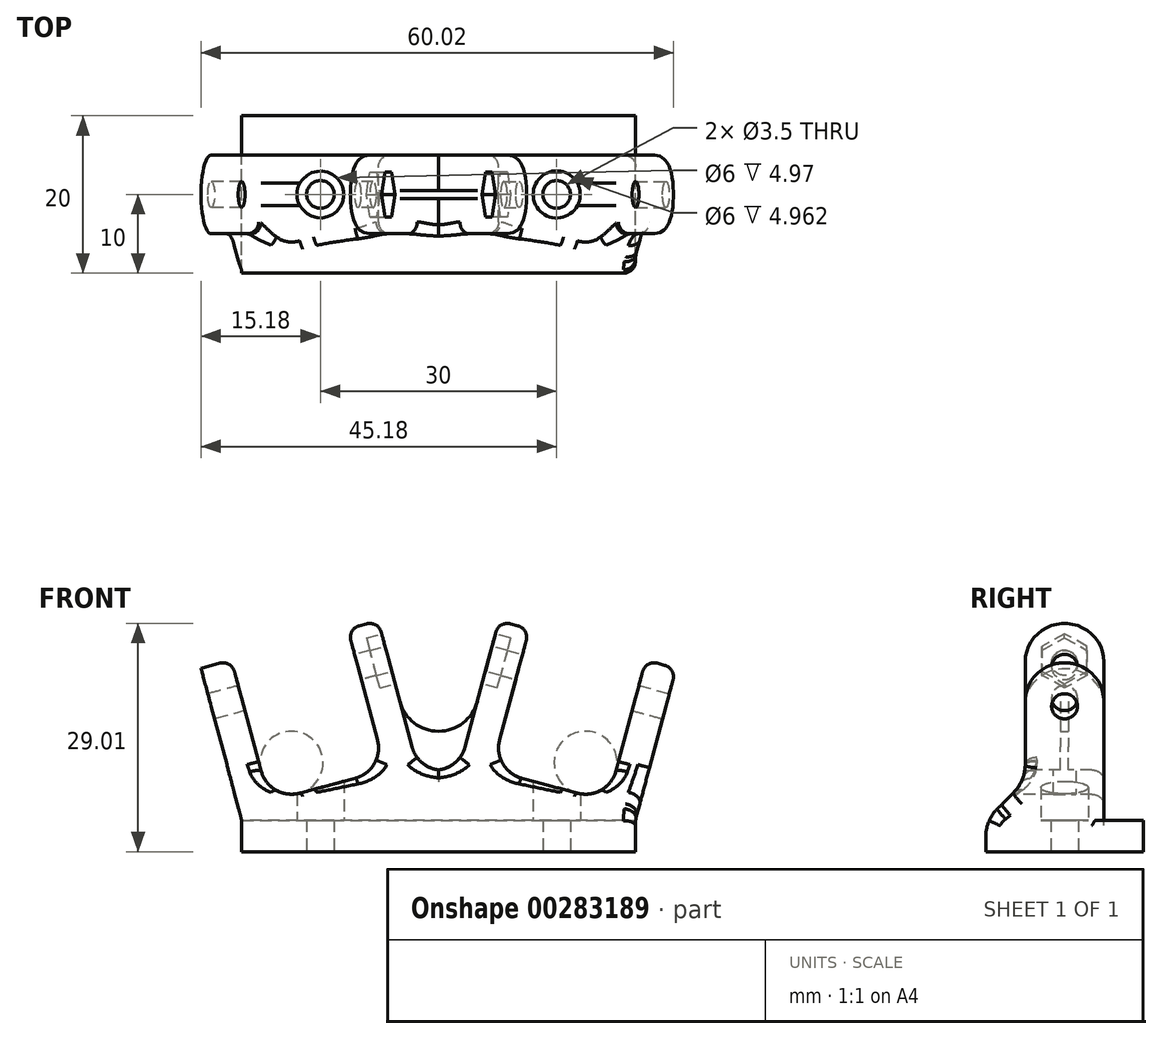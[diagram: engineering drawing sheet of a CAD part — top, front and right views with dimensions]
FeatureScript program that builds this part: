
annotation { "Feature Type Name" : "Feature", "Feature Type Description" : "" }
export const myFeature = defineFeature(function(context is Context, id is Id, definition is map)
    precondition{}
    {
        {
            var Q0;
            Q0=qCreatedBy(makeId("Top.planeOp"),FACE);
            var sketch = newSketch(context, id + "F0", { "sketchPlane" : qUnion([Q0])});
            skLineSegment(sketch, "E0.bottom", {"start": v(0, 0) * mm, "end": v(50, 0) * mm});
            skLineSegment(sketch, "E0.top", {"start": v(0, 20) * mm, "end": v(50, 20) * mm});
            skLineSegment(sketch, "E0.left", {"start": v(0, 0) * mm, "end": v(0, 20) * mm});
            skLineSegment(sketch, "E0.right", {"start": v(50, 0) * mm, "end": v(50, 20) * mm});
            skSolve(sketch);
        }
        {
            var Q0;
            Q0 = qSketchRegion(id + "F0", true);
            extrude(context, id + "F1", {"entities" : qUnion([Q0]), "depth" : 4 * mm});
        }
        {
            var Q0;
            Q0=makeQuery(id+"F1.opExtrude","SWEPT_FACE",FACE,{"disambiguationData":[OSD([sQuery(id+"F0.wireOp",EDGE,"E0.bottom")])]});
            cPlane(context, id + "F2", {"entities" : qUnion([Q0]), "cplaneType" : CPlaneType.OFFSET, "offset" : 10 * mm, "oppositeDirection" : true, "width" : 150 * mm, "height" : 150 * mm});
        }
        {
            var Q0;
            Q0=qCreatedBy(id+"F2.planeOp",FACE);
            var sketch = newSketch(context, id + "F3", { "sketchPlane" : qUnion([Q0])});
            skLineSegment(sketch, "E1.0.0", {"start": v(0, 0) * mm, "end": v(50, 0) * mm, "construction": true});
            skLineSegment(sketch, "E1.0.1", {"start": v(50, 0) * mm, "end": v(50, 4) * mm, "construction": true});
            skLineSegment(sketch, "E1.0.2", {"start": v(50, 4) * mm, "end": v(0, 4) * mm, "construction": true});
            skLineSegment(sketch, "E1.0.3", {"start": v(0, 4) * mm, "end": v(0, 0) * mm, "construction": true});
            skLineSegment(sketch, "E2", {"start": v(0, 4) * mm, "end": v(-5.18, 23.32) * mm});
            skLineSegment(sketch, "E3", {"start": v(-5.18, 23.32) * mm, "end": v(-1.31, 24.35) * mm});
            skLineSegment(sketch, "E4", {"start": v(-1.31, 24.35) * mm, "end": v(3.5, 6.41) * mm});
            skLineSegment(sketch, "E5", {"start": v(4.14, 4) * mm, "end": v(0, 4) * mm});
            skLineSegment(sketch, "E6", {"start": v(25, 4) * mm, "end": v(25, 45.14) * mm, "construction": true});
            skLineSegment(sketch, "E7", {"start": v(-5.18, 23.32) * mm, "end": v(32.1, 33.3) * mm, "construction": true});
            skLineSegment(sketch, "E8", {"start": v(22.41, 10.37) * mm, "end": v(17.33, 29.35) * mm});
            skLineSegment(sketch, "E9", {"start": v(17.33, 29.35) * mm, "end": v(13.47, 28.31) * mm});
            skLineSegment(sketch, "E10", {"start": v(13.47, 28.31) * mm, "end": v(18.27, 10.37) * mm});
            skLineSegment(sketch, "E11", {"start": v(19.98, 4) * mm, "end": v(24.12, 4) * mm});
            skLineSegment(sketch, "E12", {"start": v(3.5, 6.41) * mm, "end": v(18.27, 10.37) * mm});
            skLineSegment(sketch, "E13", {"start": v(4.14, 4) * mm, "end": v(19.98, 4) * mm});
            skLineSegment(sketch, "E14.MirrorCS", {"start": v(45.86, 4) * mm, "end": v(30.02, 4) * mm});
            skLineSegment(sketch, "E15.MirrorCS", {"start": v(36.53, 28.31) * mm, "end": v(31.73, 10.37) * mm});
            skLineSegment(sketch, "E16.MirrorCS", {"start": v(32.67, 29.35) * mm, "end": v(36.53, 28.31) * mm});
            skLineSegment(sketch, "E17.MirrorCS", {"start": v(46.5, 6.41) * mm, "end": v(31.73, 10.37) * mm});
            skLineSegment(sketch, "E18.MirrorCS", {"start": v(55.18, 23.32) * mm, "end": v(51.31, 24.35) * mm});
            skLineSegment(sketch, "E19.MirrorCS", {"start": v(45.86, 4) * mm, "end": v(50, 4) * mm});
            skLineSegment(sketch, "E20.MirrorCS", {"start": v(30.02, 4) * mm, "end": v(25.88, 4) * mm});
            skLineSegment(sketch, "E21.MirrorCS", {"start": v(51.31, 24.35) * mm, "end": v(46.5, 6.41) * mm});
            skLineSegment(sketch, "E22.MirrorCS", {"start": v(50, 4) * mm, "end": v(55.18, 23.32) * mm});
            skLineSegment(sketch, "E23.MirrorCS", {"start": v(27.59, 10.37) * mm, "end": v(32.67, 29.35) * mm});
            skLineSegment(sketch, "E24", {"start": v(22.41, 10.37) * mm, "end": v(27.59, 10.37) * mm});
            skLineSegment(sketch, "E25", {"start": v(24.12, 4) * mm, "end": v(25.88, 4) * mm});
            skSolve(sketch);
        }
        {
            var Q0;
            Q0 = qSketchRegion(id + "F3", true);
            extrude(context, id + "F4", {"entities" : qUnion([Q0]), "operationType" : NewBodyOperationType.ADD, "endBound" : BoundingType.SYMMETRIC, "depth" : 10 * mm});
        }
        {
            var Q0;
            Q0=makeQuery(id+"F4.opExtrude","SWEPT_FACE",FACE,{"disambiguationData":[OSD([sQuery(id+"F3.wireOp",EDGE,"E2")])]});
            var sketch = newSketch(context, id + "F5", { "sketchPlane" : qUnion([Q0])});
            skCircle(sketch, "E26", {"center": v(-10, 18.86) * mm, "radius": 1.65 * mm});
            skPoint(sketch, "E26.centerSnap0", {"position": v(-10, 23.86) * mm});
            skSolve(sketch);
        }
        {
            var Q0;
            Q0 = qSketchRegion(id + "F5", true);
            var Q1;
            Q1=makeQuery(id+"F4.opExtrude","SWEPT_FACE",FACE,{"disambiguationData":[OSD([sQuery(id+"F3.wireOp",EDGE,"E8")])]});
            extrude(context, id + "F6", {"entities" : qUnion([Q0]), "operationType" : NewBodyOperationType.REMOVE, "endBound" : BoundingType.UP_TO_SURFACE, "oppositeDirection" : true, "endBoundEntityFace" : qUnion([Q1]), "depth" : 25 * mm});
        }
        {
            var Q0;
            Q0=makeQuery(id+"F4.opExtrude","SWEPT_FACE",FACE,{"disambiguationData":[OSD([sQuery(id+"F3.wireOp",EDGE,"E22.MirrorCS")])]});
            var sketch = newSketch(context, id + "F7", { "sketchPlane" : qUnion([Q0])});
            skCircle(sketch, "E27", {"center": v(10, 31.8) * mm, "radius": 1.65 * mm});
            skPoint(sketch, "E27.centerSnap0", {"position": v(10, 36.8) * mm});
            skSolve(sketch);
        }
        {
            var Q0;
            Q0 = qSketchRegion(id + "F7", true);
            var Q1;
            Q1=makeQuery(id+"F4.opExtrude","SWEPT_FACE",FACE,{"disambiguationData":[OSD([sQuery(id+"F3.wireOp",EDGE,"E23.MirrorCS")])]});
            extrude(context, id + "F8", {"entities" : qUnion([Q0]), "operationType" : NewBodyOperationType.REMOVE, "endBound" : BoundingType.UP_TO_SURFACE, "oppositeDirection" : true, "endBoundEntityFace" : qUnion([Q1]), "depth" : 25 * mm});
        }
        {
            var Q0;
            Q0=makeQuery(id+"F4.opExtrude","CAP_EDGE",EDGE,{"disambiguationData":[OSD([sQuery(id+"F3.wireOp",EDGE,"E5"),sQuery(id+"F3.wireOp",EDGE,"E11"),sQuery(id+"F3.wireOp",EDGE,"E13"),sQuery(id+"F3.wireOp",EDGE,"E14.MirrorCS"),sQuery(id+"F3.wireOp",EDGE,"E19.MirrorCS"),sQuery(id+"F3.wireOp",EDGE,"E20.MirrorCS"),sQuery(id+"F3.wireOp",EDGE,"E25")])],"isStart":false});
            var Q1;
            Q1=makeQuery(id+"F4.opExtrude","CAP_EDGE",EDGE,{"disambiguationData":[OSD([sQuery(id+"F3.wireOp",EDGE,"E5"),sQuery(id+"F3.wireOp",EDGE,"E11"),sQuery(id+"F3.wireOp",EDGE,"E13"),sQuery(id+"F3.wireOp",EDGE,"E14.MirrorCS"),sQuery(id+"F3.wireOp",EDGE,"E19.MirrorCS"),sQuery(id+"F3.wireOp",EDGE,"E20.MirrorCS"),sQuery(id+"F3.wireOp",EDGE,"E25")])],"isStart":true});
            chamfer(context, id + "F9", {"entities" : qUnion([Q0, Q1]), "width" : 5 * mm, "tangentPropagation" : true});
        }
        {
            var Q0;
            Q0=makeQuery(id+"F4.boolean.opBoolean","MERGE",EDGE,{"derivedFrom":[makeQuery(id+"F1.opExtrude","CAP_EDGE",EDGE,{"disambiguationData":[OSD([sQuery(id+"F0.wireOp",EDGE,"E0.right")])],"isStart":false}),makeQuery(id+"F4.opExtrude","SWEPT_EDGE",EDGE,{"disambiguationData":[OSD([sQuery(id+"F3.wireOp",EDGE,"E19.MirrorCS"),sQuery(id+"F3.wireOp",EDGE,"E22.MirrorCS")])]})]});
            var Q1;
            Q1=makeQuery(id+"F4.boolean.opBoolean","MERGE",EDGE,{"derivedFrom":[makeQuery(id+"F1.opExtrude","CAP_EDGE",EDGE,{"disambiguationData":[OSD([sQuery(id+"F0.wireOp",EDGE,"E0.left")])],"isStart":false}),makeQuery(id+"F4.opExtrude","SWEPT_EDGE",EDGE,{"disambiguationData":[OSD([sQuery(id+"F3.wireOp",EDGE,"E2"),sQuery(id+"F3.wireOp",EDGE,"E5")])]})]});
            fillet(context, id + "F10", {"entities" : qUnion([Q0, Q1]), "radius" : 5 * mm, "tangentPropagation" : true, "allowEdgeOverflow" : false});
        }
        {
            var Q0;
            Q0=makeQuery(id+"F1.opExtrude","CAP_FACE",FACE,{"disambiguationData":[OSD([sQuery(id+"F0.wireOp",EDGE,"E0.bottom"),sQuery(id+"F0.wireOp",EDGE,"E0.top"),sQuery(id+"F0.wireOp",EDGE,"E0.left"),sQuery(id+"F0.wireOp",EDGE,"E0.right")])],"isStart":true});
            var sketch = newSketch(context, id + "F11", { "sketchPlane" : qUnion([Q0])});
            skCircle(sketch, "E28", {"center": v(10, -10) * mm, "radius": 1.75 * mm});
            skPoint(sketch, "E28.centerSnap0", {"position": v(0, -10) * mm});
            skCircle(sketch, "E29", {"center": v(40, -10) * mm, "radius": 1.75 * mm});
            skSolve(sketch);
        }
        {
            var Q0;
            Q0 = qSketchRegion(id + "F11", true);
            extrude(context, id + "F12", {"entities" : qUnion([Q0]), "operationType" : NewBodyOperationType.REMOVE, "endBound" : BoundingType.UP_TO_NEXT, "oppositeDirection" : true, "depth" : 25 * mm});
        }
        {
            var Q0;
            Q0=makeQuery(id+"F1.opExtrude","CAP_FACE",FACE,{"disambiguationData":[OSD([sQuery(id+"F0.wireOp",EDGE,"E0.bottom"),sQuery(id+"F0.wireOp",EDGE,"E0.top"),sQuery(id+"F0.wireOp",EDGE,"E0.left"),sQuery(id+"F0.wireOp",EDGE,"E0.right")])],"isStart":true});
            cPlane(context, id + "F13", {"entities" : qUnion([Q0]), "cplaneType" : CPlaneType.OFFSET, "offset" : 4 * mm, "oppositeDirection" : true, "width" : 150 * mm, "height" : 150 * mm});
        }
        {
            var Q0;
            Q0=qCreatedBy(id+"F13.planeOp",FACE);
            var sketch = newSketch(context, id + "F14", { "sketchPlane" : qUnion([Q0])});
            skCircle(sketch, "E30.0", {"center": v(10, -10) * mm, "radius": 1.75 * mm, "construction": true});
            skCircle(sketch, "E31.0", {"center": v(40, -10) * mm, "radius": 1.75 * mm, "construction": true});
            skCircle(sketch, "E32", {"center": v(10, -10) * mm, "radius": 3 * mm});
            skCircle(sketch, "E33", {"center": v(40, -10) * mm, "radius": 3 * mm});
            skSolve(sketch);
        }
        {
            var Q0;
            Q0 = qSketchRegion(id + "F14", true);
            extrude(context, id + "F15", {"entities" : qUnion([Q0]), "operationType" : NewBodyOperationType.REMOVE, "oppositeDirection" : true, "depth" : 20 * mm});
        }
        {
            var Q0;
            Q0=makeQuery(id+"F4.opExtrude","CAP_EDGE",EDGE,{"disambiguationData":[OSD([sQuery(id+"F3.wireOp",EDGE,"E3")])],"isStart":true});
            var Q1;
            Q1=makeQuery(id+"F4.opExtrude","CAP_EDGE",EDGE,{"disambiguationData":[OSD([sQuery(id+"F3.wireOp",EDGE,"E3")])],"isStart":false});
            var Q2;
            Q2=makeQuery(id+"F4.opExtrude","CAP_EDGE",EDGE,{"disambiguationData":[OSD([sQuery(id+"F3.wireOp",EDGE,"E9")])],"isStart":true});
            var Q3;
            Q3=makeQuery(id+"F4.opExtrude","CAP_EDGE",EDGE,{"disambiguationData":[OSD([sQuery(id+"F3.wireOp",EDGE,"E9")])],"isStart":false});
            var Q4;
            Q4=makeQuery(id+"F4.opExtrude","CAP_EDGE",EDGE,{"disambiguationData":[OSD([sQuery(id+"F3.wireOp",EDGE,"E16.MirrorCS")])],"isStart":true});
            var Q5;
            Q5=makeQuery(id+"F4.opExtrude","CAP_EDGE",EDGE,{"disambiguationData":[OSD([sQuery(id+"F3.wireOp",EDGE,"E16.MirrorCS")])],"isStart":false});
            var Q6;
            Q6=makeQuery(id+"F4.opExtrude","CAP_EDGE",EDGE,{"disambiguationData":[OSD([sQuery(id+"F3.wireOp",EDGE,"E18.MirrorCS")])],"isStart":false});
            var Q7;
            Q7=makeQuery(id+"F4.opExtrude","CAP_EDGE",EDGE,{"disambiguationData":[OSD([sQuery(id+"F3.wireOp",EDGE,"E18.MirrorCS")])],"isStart":true});
            fillet(context, id + "F16", {"entities" : qUnion([Q0, Q1, Q2, Q3, Q4, Q5, Q6, Q7]), "radius" : 5 * mm, "tangentPropagation" : true, "allowEdgeOverflow" : false});
        }
        {
            var Q0;
            Q0=makeQuery(id+"F4.opExtrude","SWEPT_FACE",FACE,{"disambiguationData":[OSD([sQuery(id+"F3.wireOp",EDGE,"E8")])]});
            var sketch = newSketch(context, id + "F17", { "sketchPlane" : qUnion([Q0])});
            skCircle(sketch, "E34.cCircle", {"center": v(10, 18.86) * mm, "radius": 2.85 * mm, "construction": true});
            skLineSegment(sketch, "E34.0", {"start": v(10, 22.15) * mm, "end": v(12.85, 20.5) * mm});
            skLineSegment(sketch, "E34.1", {"start": v(12.85, 20.5) * mm, "end": v(12.85, 17.22) * mm});
            skLineSegment(sketch, "E34.2", {"start": v(12.85, 17.22) * mm, "end": v(10, 15.57) * mm});
            skLineSegment(sketch, "E34.3", {"start": v(10, 15.57) * mm, "end": v(7.15, 17.22) * mm});
            skLineSegment(sketch, "E34.4", {"start": v(7.15, 17.22) * mm, "end": v(7.15, 20.5) * mm});
            skLineSegment(sketch, "E34.5", {"start": v(7.15, 20.5) * mm, "end": v(10, 22.15) * mm});
            skPoint(sketch, "E34.0.midPoint", {"position": v(11.42, 21.33) * mm});
            skSolve(sketch);
        }
        {
            var Q0;
            Q0 = qSketchRegion(id + "F17", true);
            extrude(context, id + "F18", {"entities" : qUnion([Q0]), "operationType" : NewBodyOperationType.REMOVE, "oppositeDirection" : true, "depth" : 2 * mm});
        }
        {
            var Q0;
            Q0=makeQuery(id+"F4.opExtrude","SWEPT_FACE",FACE,{"disambiguationData":[OSD([sQuery(id+"F3.wireOp",EDGE,"E23.MirrorCS")])]});
            var sketch = newSketch(context, id + "F19", { "sketchPlane" : qUnion([Q0])});
            skCircle(sketch, "E35.cCircle", {"center": v(-10, 31.8) * mm, "radius": 2.85 * mm, "construction": true});
            skLineSegment(sketch, "E35.0", {"start": v(-7.15, 33.45) * mm, "end": v(-7.15, 30.16) * mm});
            skLineSegment(sketch, "E35.1", {"start": v(-7.15, 30.16) * mm, "end": v(-10, 28.51) * mm});
            skLineSegment(sketch, "E35.2", {"start": v(-10, 28.51) * mm, "end": v(-12.85, 30.16) * mm});
            skLineSegment(sketch, "E35.3", {"start": v(-12.85, 30.16) * mm, "end": v(-12.85, 33.45) * mm});
            skLineSegment(sketch, "E35.4", {"start": v(-12.85, 33.45) * mm, "end": v(-10, 35.1) * mm});
            skLineSegment(sketch, "E35.5", {"start": v(-10, 35.1) * mm, "end": v(-7.15, 33.45) * mm});
            skPoint(sketch, "E35.0.midPoint", {"position": v(-7.15, 31.8) * mm});
            skSolve(sketch);
        }
        {
            var Q0;
            Q0 = qSketchRegion(id + "F19", true);
            extrude(context, id + "F20", {"entities" : qUnion([Q0]), "operationType" : NewBodyOperationType.REMOVE, "oppositeDirection" : true, "depth" : 2 * mm});
        }
        {
            var Q0;
            Q0=makeQuery(id+"F9.opChamfer","BLEND_EDGE",EDGE,{"blendedFrom":[makeQuery(id+"F4.opExtrude","CAP_EDGE",EDGE,{"disambiguationData":[OSD([sQuery(id+"F3.wireOp",EDGE,"E5"),sQuery(id+"F3.wireOp",EDGE,"E11"),sQuery(id+"F3.wireOp",EDGE,"E13"),sQuery(id+"F3.wireOp",EDGE,"E14.MirrorCS"),sQuery(id+"F3.wireOp",EDGE,"E19.MirrorCS"),sQuery(id+"F3.wireOp",EDGE,"E20.MirrorCS"),sQuery(id+"F3.wireOp",EDGE,"E25")])],"isStart":false}),makeQuery(id+"F1.opExtrude","SWEPT_FACE",FACE,{"disambiguationData":[OSD([sQuery(id+"F0.wireOp",EDGE,"E0.bottom")])]})],"blendedInto":[makeQuery(id+"F1.opExtrude","SWEPT_FACE",FACE,{"disambiguationData":[OSD([sQuery(id+"F0.wireOp",EDGE,"E0.bottom")])]})]});
            var Q1;
            Q1=makeQuery(id+"F9.opChamfer","BLEND_EDGE",EDGE,{"blendedFrom":[makeQuery(id+"F4.opExtrude","CAP_EDGE",EDGE,{"disambiguationData":[OSD([sQuery(id+"F3.wireOp",EDGE,"E5"),sQuery(id+"F3.wireOp",EDGE,"E11"),sQuery(id+"F3.wireOp",EDGE,"E13"),sQuery(id+"F3.wireOp",EDGE,"E14.MirrorCS"),sQuery(id+"F3.wireOp",EDGE,"E19.MirrorCS"),sQuery(id+"F3.wireOp",EDGE,"E20.MirrorCS"),sQuery(id+"F3.wireOp",EDGE,"E25")])],"isStart":true}),makeQuery(id+"F1.opExtrude","SWEPT_FACE",FACE,{"disambiguationData":[OSD([sQuery(id+"F0.wireOp",EDGE,"E0.top")])]})],"blendedInto":[makeQuery(id+"F1.opExtrude","SWEPT_FACE",FACE,{"disambiguationData":[OSD([sQuery(id+"F0.wireOp",EDGE,"E0.top")])]})]});
            var Q2;
            {var subQ0=sQuery(id+"F3.wireOp",EDGE,"E25");var subQ1=sQuery(id+"F3.wireOp",EDGE,"E20.MirrorCS");var subQ2=sQuery(id+"F3.wireOp",EDGE,"E19.MirrorCS");var subQ3=sQuery(id+"F3.wireOp",EDGE,"E14.MirrorCS");var subQ4=sQuery(id+"F3.wireOp",EDGE,"E13");var subQ5=sQuery(id+"F3.wireOp",EDGE,"E11");var subQ6=sQuery(id+"F3.wireOp",EDGE,"E5");Q2=makeQuery(id+"F9.opChamfer","BLEND_EDGE",EDGE,{"disambiguationData":[OD(0.0)],"blendedFrom":[makeQuery(id+"F4.opExtrude","CAP_EDGE",EDGE,{"disambiguationData":[OSD([subQ6,subQ5,subQ4,subQ3,subQ2,subQ1,subQ0])],"isStart":false}),makeQuery(id+"F4.opExtrude","CAP_FACE",FACE,{"disambiguationData":[OSD([sQuery(id+"F3.wireOp",EDGE,"E2"),sQuery(id+"F3.wireOp",EDGE,"E3"),sQuery(id+"F3.wireOp",EDGE,"E4"),subQ6,sQuery(id+"F3.wireOp",EDGE,"E8"),sQuery(id+"F3.wireOp",EDGE,"E9"),sQuery(id+"F3.wireOp",EDGE,"E10"),subQ5,sQuery(id+"F3.wireOp",EDGE,"E12"),subQ4,subQ3,sQuery(id+"F3.wireOp",EDGE,"E15.MirrorCS"),sQuery(id+"F3.wireOp",EDGE,"E16.MirrorCS"),sQuery(id+"F3.wireOp",EDGE,"E17.MirrorCS"),sQuery(id+"F3.wireOp",EDGE,"E18.MirrorCS"),subQ2,subQ1,sQuery(id+"F3.wireOp",EDGE,"E21.MirrorCS"),sQuery(id+"F3.wireOp",EDGE,"E22.MirrorCS"),sQuery(id+"F3.wireOp",EDGE,"E23.MirrorCS"),sQuery(id+"F3.wireOp",EDGE,"E24"),subQ0])],"isStart":false})],"blendedInto":[makeQuery(id+"F4.opExtrude","CAP_FACE",FACE,{"disambiguationData":[OSD([sQuery(id+"F3.wireOp",EDGE,"E2"),sQuery(id+"F3.wireOp",EDGE,"E3"),sQuery(id+"F3.wireOp",EDGE,"E4"),subQ6,sQuery(id+"F3.wireOp",EDGE,"E8"),sQuery(id+"F3.wireOp",EDGE,"E9"),sQuery(id+"F3.wireOp",EDGE,"E10"),subQ5,sQuery(id+"F3.wireOp",EDGE,"E12"),subQ4,subQ3,sQuery(id+"F3.wireOp",EDGE,"E15.MirrorCS"),sQuery(id+"F3.wireOp",EDGE,"E16.MirrorCS"),sQuery(id+"F3.wireOp",EDGE,"E17.MirrorCS"),sQuery(id+"F3.wireOp",EDGE,"E18.MirrorCS"),subQ2,subQ1,sQuery(id+"F3.wireOp",EDGE,"E21.MirrorCS"),sQuery(id+"F3.wireOp",EDGE,"E22.MirrorCS"),sQuery(id+"F3.wireOp",EDGE,"E23.MirrorCS"),sQuery(id+"F3.wireOp",EDGE,"E24"),subQ0])],"isStart":false})]});}
            var Q3;
            {var subQ0=sQuery(id+"F3.wireOp",EDGE,"E25");var subQ1=sQuery(id+"F3.wireOp",EDGE,"E20.MirrorCS");var subQ2=sQuery(id+"F3.wireOp",EDGE,"E19.MirrorCS");var subQ3=sQuery(id+"F3.wireOp",EDGE,"E14.MirrorCS");var subQ4=sQuery(id+"F3.wireOp",EDGE,"E13");var subQ5=sQuery(id+"F3.wireOp",EDGE,"E11");var subQ6=sQuery(id+"F3.wireOp",EDGE,"E5");Q3=makeQuery(id+"F9.opChamfer","BLEND_EDGE",EDGE,{"disambiguationData":[OD(0.0)],"blendedFrom":[makeQuery(id+"F4.opExtrude","CAP_EDGE",EDGE,{"disambiguationData":[OSD([subQ6,subQ5,subQ4,subQ3,subQ2,subQ1,subQ0])],"isStart":true}),makeQuery(id+"F4.opExtrude","CAP_FACE",FACE,{"disambiguationData":[OSD([sQuery(id+"F3.wireOp",EDGE,"E2"),sQuery(id+"F3.wireOp",EDGE,"E3"),sQuery(id+"F3.wireOp",EDGE,"E4"),subQ6,sQuery(id+"F3.wireOp",EDGE,"E8"),sQuery(id+"F3.wireOp",EDGE,"E9"),sQuery(id+"F3.wireOp",EDGE,"E10"),subQ5,sQuery(id+"F3.wireOp",EDGE,"E12"),subQ4,subQ3,sQuery(id+"F3.wireOp",EDGE,"E15.MirrorCS"),sQuery(id+"F3.wireOp",EDGE,"E16.MirrorCS"),sQuery(id+"F3.wireOp",EDGE,"E17.MirrorCS"),sQuery(id+"F3.wireOp",EDGE,"E18.MirrorCS"),subQ2,subQ1,sQuery(id+"F3.wireOp",EDGE,"E21.MirrorCS"),sQuery(id+"F3.wireOp",EDGE,"E22.MirrorCS"),sQuery(id+"F3.wireOp",EDGE,"E23.MirrorCS"),sQuery(id+"F3.wireOp",EDGE,"E24"),subQ0])],"isStart":true})],"blendedInto":[makeQuery(id+"F4.opExtrude","CAP_FACE",FACE,{"disambiguationData":[OSD([sQuery(id+"F3.wireOp",EDGE,"E2"),sQuery(id+"F3.wireOp",EDGE,"E3"),sQuery(id+"F3.wireOp",EDGE,"E4"),subQ6,sQuery(id+"F3.wireOp",EDGE,"E8"),sQuery(id+"F3.wireOp",EDGE,"E9"),sQuery(id+"F3.wireOp",EDGE,"E10"),subQ5,sQuery(id+"F3.wireOp",EDGE,"E12"),subQ4,subQ3,sQuery(id+"F3.wireOp",EDGE,"E15.MirrorCS"),sQuery(id+"F3.wireOp",EDGE,"E16.MirrorCS"),sQuery(id+"F3.wireOp",EDGE,"E17.MirrorCS"),sQuery(id+"F3.wireOp",EDGE,"E18.MirrorCS"),subQ2,subQ1,sQuery(id+"F3.wireOp",EDGE,"E21.MirrorCS"),sQuery(id+"F3.wireOp",EDGE,"E22.MirrorCS"),sQuery(id+"F3.wireOp",EDGE,"E23.MirrorCS"),sQuery(id+"F3.wireOp",EDGE,"E24"),subQ0])],"isStart":true})]});}
            fillet(context, id + "F21", {"entities" : qUnion([Q0, Q1, Q2, Q3]), "radius" : 5 * mm, "tangentPropagation" : true, "allowEdgeOverflow" : false});
        }
        {
            var Q0;
            Q0=makeQuery(id+"F4.opExtrude","SWEPT_EDGE",EDGE,{"disambiguationData":[OSD([sQuery(id+"F3.wireOp",EDGE,"E4"),sQuery(id+"F3.wireOp",EDGE,"E12")])]});
            var Q1;
            Q1=makeQuery(id+"F4.opExtrude","SWEPT_EDGE",EDGE,{"disambiguationData":[OSD([sQuery(id+"F3.wireOp",EDGE,"E10"),sQuery(id+"F3.wireOp",EDGE,"E12")])]});
            var Q2;
            Q2=makeQuery(id+"F4.opExtrude","SWEPT_EDGE",EDGE,{"disambiguationData":[OSD([sQuery(id+"F3.wireOp",EDGE,"E23.MirrorCS"),sQuery(id+"F3.wireOp",EDGE,"E24")])]});
            var Q3;
            Q3=makeQuery(id+"F4.opExtrude","SWEPT_EDGE",EDGE,{"disambiguationData":[OSD([sQuery(id+"F3.wireOp",EDGE,"E17.MirrorCS"),sQuery(id+"F3.wireOp",EDGE,"E21.MirrorCS")])]});
            var Q4;
            Q4=makeQuery(id+"F4.opExtrude","SWEPT_EDGE",EDGE,{"disambiguationData":[OSD([sQuery(id+"F3.wireOp",EDGE,"E8"),sQuery(id+"F3.wireOp",EDGE,"E24")])]});
            var Q5;
            Q5=makeQuery(id+"F4.opExtrude","SWEPT_EDGE",EDGE,{"disambiguationData":[OSD([sQuery(id+"F3.wireOp",EDGE,"E15.MirrorCS"),sQuery(id+"F3.wireOp",EDGE,"E17.MirrorCS")])]});
            fillet(context, id + "F22", {"entities" : qUnion([Q0, Q1, Q2, Q3, Q4, Q5]), "radius" : 4 * mm, "tangentPropagation" : true, "allowEdgeOverflow" : false});
        }
        {
            var Q0;
            {var subQ0=sQuery(id+"F3.wireOp",EDGE,"E25");var subQ1=sQuery(id+"F3.wireOp",EDGE,"E20.MirrorCS");var subQ2=sQuery(id+"F3.wireOp",EDGE,"E19.MirrorCS");var subQ3=sQuery(id+"F3.wireOp",EDGE,"E14.MirrorCS");var subQ4=sQuery(id+"F3.wireOp",EDGE,"E13");var subQ5=sQuery(id+"F3.wireOp",EDGE,"E11");var subQ6=sQuery(id+"F3.wireOp",EDGE,"E5");Q0=makeQuery(id+"F9.opChamfer","BLEND_EDGE",EDGE,{"disambiguationData":[OD(2.0)],"blendedFrom":[makeQuery(id+"F4.opExtrude","CAP_EDGE",EDGE,{"disambiguationData":[OSD([subQ6,subQ5,subQ4,subQ3,subQ2,subQ1,subQ0])],"isStart":false}),makeQuery(id+"F4.opExtrude","CAP_FACE",FACE,{"disambiguationData":[OSD([sQuery(id+"F3.wireOp",EDGE,"E2"),sQuery(id+"F3.wireOp",EDGE,"E3"),sQuery(id+"F3.wireOp",EDGE,"E4"),subQ6,sQuery(id+"F3.wireOp",EDGE,"E8"),sQuery(id+"F3.wireOp",EDGE,"E9"),sQuery(id+"F3.wireOp",EDGE,"E10"),subQ5,sQuery(id+"F3.wireOp",EDGE,"E12"),subQ4,subQ3,sQuery(id+"F3.wireOp",EDGE,"E15.MirrorCS"),sQuery(id+"F3.wireOp",EDGE,"E16.MirrorCS"),sQuery(id+"F3.wireOp",EDGE,"E17.MirrorCS"),sQuery(id+"F3.wireOp",EDGE,"E18.MirrorCS"),subQ2,subQ1,sQuery(id+"F3.wireOp",EDGE,"E21.MirrorCS"),sQuery(id+"F3.wireOp",EDGE,"E22.MirrorCS"),sQuery(id+"F3.wireOp",EDGE,"E23.MirrorCS"),sQuery(id+"F3.wireOp",EDGE,"E24"),subQ0])],"isStart":false})],"blendedInto":[makeQuery(id+"F4.opExtrude","CAP_FACE",FACE,{"disambiguationData":[OSD([sQuery(id+"F3.wireOp",EDGE,"E2"),sQuery(id+"F3.wireOp",EDGE,"E3"),sQuery(id+"F3.wireOp",EDGE,"E4"),subQ6,sQuery(id+"F3.wireOp",EDGE,"E8"),sQuery(id+"F3.wireOp",EDGE,"E9"),sQuery(id+"F3.wireOp",EDGE,"E10"),subQ5,sQuery(id+"F3.wireOp",EDGE,"E12"),subQ4,subQ3,sQuery(id+"F3.wireOp",EDGE,"E15.MirrorCS"),sQuery(id+"F3.wireOp",EDGE,"E16.MirrorCS"),sQuery(id+"F3.wireOp",EDGE,"E17.MirrorCS"),sQuery(id+"F3.wireOp",EDGE,"E18.MirrorCS"),subQ2,subQ1,sQuery(id+"F3.wireOp",EDGE,"E21.MirrorCS"),sQuery(id+"F3.wireOp",EDGE,"E22.MirrorCS"),sQuery(id+"F3.wireOp",EDGE,"E23.MirrorCS"),sQuery(id+"F3.wireOp",EDGE,"E24"),subQ0])],"isStart":false})]});}
            var Q1;
            {var subQ0=sQuery(id+"F3.wireOp",EDGE,"E25");var subQ1=sQuery(id+"F3.wireOp",EDGE,"E20.MirrorCS");var subQ2=sQuery(id+"F3.wireOp",EDGE,"E19.MirrorCS");var subQ3=sQuery(id+"F3.wireOp",EDGE,"E14.MirrorCS");var subQ4=sQuery(id+"F3.wireOp",EDGE,"E13");var subQ5=sQuery(id+"F3.wireOp",EDGE,"E11");var subQ6=sQuery(id+"F3.wireOp",EDGE,"E5");Q1=makeQuery(id+"F9.opChamfer","BLEND_EDGE",EDGE,{"disambiguationData":[OD(1.0)],"blendedFrom":[makeQuery(id+"F4.opExtrude","CAP_EDGE",EDGE,{"disambiguationData":[OSD([subQ6,subQ5,subQ4,subQ3,subQ2,subQ1,subQ0])],"isStart":false}),makeQuery(id+"F4.opExtrude","CAP_FACE",FACE,{"disambiguationData":[OSD([sQuery(id+"F3.wireOp",EDGE,"E2"),sQuery(id+"F3.wireOp",EDGE,"E3"),sQuery(id+"F3.wireOp",EDGE,"E4"),subQ6,sQuery(id+"F3.wireOp",EDGE,"E8"),sQuery(id+"F3.wireOp",EDGE,"E9"),sQuery(id+"F3.wireOp",EDGE,"E10"),subQ5,sQuery(id+"F3.wireOp",EDGE,"E12"),subQ4,subQ3,sQuery(id+"F3.wireOp",EDGE,"E15.MirrorCS"),sQuery(id+"F3.wireOp",EDGE,"E16.MirrorCS"),sQuery(id+"F3.wireOp",EDGE,"E17.MirrorCS"),sQuery(id+"F3.wireOp",EDGE,"E18.MirrorCS"),subQ2,subQ1,sQuery(id+"F3.wireOp",EDGE,"E21.MirrorCS"),sQuery(id+"F3.wireOp",EDGE,"E22.MirrorCS"),sQuery(id+"F3.wireOp",EDGE,"E23.MirrorCS"),sQuery(id+"F3.wireOp",EDGE,"E24"),subQ0])],"isStart":false})],"blendedInto":[makeQuery(id+"F4.opExtrude","CAP_FACE",FACE,{"disambiguationData":[OSD([sQuery(id+"F3.wireOp",EDGE,"E2"),sQuery(id+"F3.wireOp",EDGE,"E3"),sQuery(id+"F3.wireOp",EDGE,"E4"),subQ6,sQuery(id+"F3.wireOp",EDGE,"E8"),sQuery(id+"F3.wireOp",EDGE,"E9"),sQuery(id+"F3.wireOp",EDGE,"E10"),subQ5,sQuery(id+"F3.wireOp",EDGE,"E12"),subQ4,subQ3,sQuery(id+"F3.wireOp",EDGE,"E15.MirrorCS"),sQuery(id+"F3.wireOp",EDGE,"E16.MirrorCS"),sQuery(id+"F3.wireOp",EDGE,"E17.MirrorCS"),sQuery(id+"F3.wireOp",EDGE,"E18.MirrorCS"),subQ2,subQ1,sQuery(id+"F3.wireOp",EDGE,"E21.MirrorCS"),sQuery(id+"F3.wireOp",EDGE,"E22.MirrorCS"),sQuery(id+"F3.wireOp",EDGE,"E23.MirrorCS"),sQuery(id+"F3.wireOp",EDGE,"E24"),subQ0])],"isStart":false})]});}
            var Q2;
            {var subQ0=sQuery(id+"F3.wireOp",EDGE,"E25");var subQ1=sQuery(id+"F3.wireOp",EDGE,"E20.MirrorCS");var subQ2=sQuery(id+"F3.wireOp",EDGE,"E19.MirrorCS");var subQ3=sQuery(id+"F3.wireOp",EDGE,"E14.MirrorCS");var subQ4=sQuery(id+"F3.wireOp",EDGE,"E13");var subQ5=sQuery(id+"F3.wireOp",EDGE,"E11");var subQ6=sQuery(id+"F3.wireOp",EDGE,"E5");Q2=makeQuery(id+"F9.opChamfer","BLEND_EDGE",EDGE,{"disambiguationData":[OD(1.0)],"blendedFrom":[makeQuery(id+"F4.opExtrude","CAP_EDGE",EDGE,{"disambiguationData":[OSD([subQ6,subQ5,subQ4,subQ3,subQ2,subQ1,subQ0])],"isStart":true}),makeQuery(id+"F4.opExtrude","CAP_FACE",FACE,{"disambiguationData":[OSD([sQuery(id+"F3.wireOp",EDGE,"E2"),sQuery(id+"F3.wireOp",EDGE,"E3"),sQuery(id+"F3.wireOp",EDGE,"E4"),subQ6,sQuery(id+"F3.wireOp",EDGE,"E8"),sQuery(id+"F3.wireOp",EDGE,"E9"),sQuery(id+"F3.wireOp",EDGE,"E10"),subQ5,sQuery(id+"F3.wireOp",EDGE,"E12"),subQ4,subQ3,sQuery(id+"F3.wireOp",EDGE,"E15.MirrorCS"),sQuery(id+"F3.wireOp",EDGE,"E16.MirrorCS"),sQuery(id+"F3.wireOp",EDGE,"E17.MirrorCS"),sQuery(id+"F3.wireOp",EDGE,"E18.MirrorCS"),subQ2,subQ1,sQuery(id+"F3.wireOp",EDGE,"E21.MirrorCS"),sQuery(id+"F3.wireOp",EDGE,"E22.MirrorCS"),sQuery(id+"F3.wireOp",EDGE,"E23.MirrorCS"),sQuery(id+"F3.wireOp",EDGE,"E24"),subQ0])],"isStart":true})],"blendedInto":[makeQuery(id+"F4.opExtrude","CAP_FACE",FACE,{"disambiguationData":[OSD([sQuery(id+"F3.wireOp",EDGE,"E2"),sQuery(id+"F3.wireOp",EDGE,"E3"),sQuery(id+"F3.wireOp",EDGE,"E4"),subQ6,sQuery(id+"F3.wireOp",EDGE,"E8"),sQuery(id+"F3.wireOp",EDGE,"E9"),sQuery(id+"F3.wireOp",EDGE,"E10"),subQ5,sQuery(id+"F3.wireOp",EDGE,"E12"),subQ4,subQ3,sQuery(id+"F3.wireOp",EDGE,"E15.MirrorCS"),sQuery(id+"F3.wireOp",EDGE,"E16.MirrorCS"),sQuery(id+"F3.wireOp",EDGE,"E17.MirrorCS"),sQuery(id+"F3.wireOp",EDGE,"E18.MirrorCS"),subQ2,subQ1,sQuery(id+"F3.wireOp",EDGE,"E21.MirrorCS"),sQuery(id+"F3.wireOp",EDGE,"E22.MirrorCS"),sQuery(id+"F3.wireOp",EDGE,"E23.MirrorCS"),sQuery(id+"F3.wireOp",EDGE,"E24"),subQ0])],"isStart":true})]});}
            var Q3;
            {var subQ0=sQuery(id+"F3.wireOp",EDGE,"E25");var subQ1=sQuery(id+"F3.wireOp",EDGE,"E20.MirrorCS");var subQ2=sQuery(id+"F3.wireOp",EDGE,"E19.MirrorCS");var subQ3=sQuery(id+"F3.wireOp",EDGE,"E14.MirrorCS");var subQ4=sQuery(id+"F3.wireOp",EDGE,"E13");var subQ5=sQuery(id+"F3.wireOp",EDGE,"E11");var subQ6=sQuery(id+"F3.wireOp",EDGE,"E5");Q3=makeQuery(id+"F9.opChamfer","BLEND_EDGE",EDGE,{"disambiguationData":[OD(2.0)],"blendedFrom":[makeQuery(id+"F4.opExtrude","CAP_EDGE",EDGE,{"disambiguationData":[OSD([subQ6,subQ5,subQ4,subQ3,subQ2,subQ1,subQ0])],"isStart":true}),makeQuery(id+"F4.opExtrude","CAP_FACE",FACE,{"disambiguationData":[OSD([sQuery(id+"F3.wireOp",EDGE,"E2"),sQuery(id+"F3.wireOp",EDGE,"E3"),sQuery(id+"F3.wireOp",EDGE,"E4"),subQ6,sQuery(id+"F3.wireOp",EDGE,"E8"),sQuery(id+"F3.wireOp",EDGE,"E9"),sQuery(id+"F3.wireOp",EDGE,"E10"),subQ5,sQuery(id+"F3.wireOp",EDGE,"E12"),subQ4,subQ3,sQuery(id+"F3.wireOp",EDGE,"E15.MirrorCS"),sQuery(id+"F3.wireOp",EDGE,"E16.MirrorCS"),sQuery(id+"F3.wireOp",EDGE,"E17.MirrorCS"),sQuery(id+"F3.wireOp",EDGE,"E18.MirrorCS"),subQ2,subQ1,sQuery(id+"F3.wireOp",EDGE,"E21.MirrorCS"),sQuery(id+"F3.wireOp",EDGE,"E22.MirrorCS"),sQuery(id+"F3.wireOp",EDGE,"E23.MirrorCS"),sQuery(id+"F3.wireOp",EDGE,"E24"),subQ0])],"isStart":true})],"blendedInto":[makeQuery(id+"F4.opExtrude","CAP_FACE",FACE,{"disambiguationData":[OSD([sQuery(id+"F3.wireOp",EDGE,"E2"),sQuery(id+"F3.wireOp",EDGE,"E3"),sQuery(id+"F3.wireOp",EDGE,"E4"),subQ6,sQuery(id+"F3.wireOp",EDGE,"E8"),sQuery(id+"F3.wireOp",EDGE,"E9"),sQuery(id+"F3.wireOp",EDGE,"E10"),subQ5,sQuery(id+"F3.wireOp",EDGE,"E12"),subQ4,subQ3,sQuery(id+"F3.wireOp",EDGE,"E15.MirrorCS"),sQuery(id+"F3.wireOp",EDGE,"E16.MirrorCS"),sQuery(id+"F3.wireOp",EDGE,"E17.MirrorCS"),sQuery(id+"F3.wireOp",EDGE,"E18.MirrorCS"),subQ2,subQ1,sQuery(id+"F3.wireOp",EDGE,"E21.MirrorCS"),sQuery(id+"F3.wireOp",EDGE,"E22.MirrorCS"),sQuery(id+"F3.wireOp",EDGE,"E23.MirrorCS"),sQuery(id+"F3.wireOp",EDGE,"E24"),subQ0])],"isStart":true})]});}
            fillet(context, id + "F23", {"entities" : qUnion([Q0, Q1, Q2, Q3]), "radius" : 5 * mm, "tangentPropagation" : true, "allowEdgeOverflow" : false});
        }
        {
            var Q0;
            Q0=makeQuery(id+"F16.opFillet","BLEND_EDGE",EDGE,{"blendedFrom":[makeQuery(id+"F4.opExtrude","CAP_EDGE",EDGE,{"disambiguationData":[OSD([sQuery(id+"F3.wireOp",EDGE,"E3")])],"isStart":false}),makeQuery(id+"F4.opExtrude","SWEPT_FACE",FACE,{"disambiguationData":[OSD([sQuery(id+"F3.wireOp",EDGE,"E2")])]})],"blendedInto":[makeQuery(id+"F4.opExtrude","SWEPT_FACE",FACE,{"disambiguationData":[OSD([sQuery(id+"F3.wireOp",EDGE,"E2")])]})]});
            var Q1;
            Q1=makeQuery(id+"F4.opExtrude","CAP_EDGE",EDGE,{"disambiguationData":[OSD([sQuery(id+"F3.wireOp",EDGE,"E10")])],"isStart":false});
            var Q2;
            Q2=makeQuery(id+"F4.opExtrude","CAP_EDGE",EDGE,{"disambiguationData":[OSD([sQuery(id+"F3.wireOp",EDGE,"E23.MirrorCS")])],"isStart":false});
            var Q3;
            Q3=makeQuery(id+"F4.opExtrude","CAP_EDGE",EDGE,{"disambiguationData":[OSD([sQuery(id+"F3.wireOp",EDGE,"E8")])],"isStart":true});
            var Q4;
            Q4=makeQuery(id+"F4.opExtrude","CAP_EDGE",EDGE,{"disambiguationData":[OSD([sQuery(id+"F3.wireOp",EDGE,"E15.MirrorCS")])],"isStart":true});
            var Q5;
            Q5=makeQuery(id+"F4.opExtrude","CAP_EDGE",EDGE,{"disambiguationData":[OSD([sQuery(id+"F3.wireOp",EDGE,"E22.MirrorCS")])],"isStart":true});
            fillet(context, id + "F24", {"entities" : qUnion([Q0, Q1, Q2, Q3, Q4, Q5]), "radius" : 1.5 * mm, "tangentPropagation" : true, "allowEdgeOverflow" : false});
        }
        {
            var Q0;
            Q0=qCreatedBy(id+"F2.planeOp",FACE);
            var sketch = newSketch(context, id + "F25", { "sketchPlane" : qUnion([Q0])});
            skArc(sketch, "E36.0.0", {"start": v(28.38, 13.34) * mm, "mid": v(28.11, 12.62) * mm, "end": v(27.71, 11.97) * mm});
            skArc(sketch, "E36.0.1", {"start": v(25, 10.4) * mm, "mid": v(26.52, 10.91) * mm, "end": v(27.71, 11.97) * mm});
            skArc(sketch, "E36.0.3", {"start": v(25, 10.4) * mm, "mid": v(26.52, 10.91) * mm, "end": v(27.71, 11.97) * mm});
            skArc(sketch, "E36.0.4", {"start": v(27.71, 11.97) * mm, "mid": v(28.11, 12.62) * mm, "end": v(28.38, 13.34) * mm});
            skArc(sketch, "E37.0.0", {"start": v(21.62, 13.34) * mm, "mid": v(21.89, 12.62) * mm, "end": v(22.29, 11.97) * mm});
            skArc(sketch, "E37.0.1", {"start": v(25, 10.4) * mm, "mid": v(23.48, 10.91) * mm, "end": v(22.29, 11.97) * mm});
            skArc(sketch, "E37.0.3", {"start": v(25, 10.4) * mm, "mid": v(23.48, 10.91) * mm, "end": v(22.29, 11.97) * mm});
            skArc(sketch, "E37.0.4", {"start": v(22.29, 11.97) * mm, "mid": v(21.89, 12.62) * mm, "end": v(21.62, 13.34) * mm});
            skLineSegment(sketch, "E38.0.1", {"start": v(29.92, 19.09) * mm, "end": v(28.38, 13.34) * mm});
            skLineSegment(sketch, "E38.0.3", {"start": v(28.38, 13.34) * mm, "end": v(29.92, 19.09) * mm});
            skLineSegment(sketch, "E39.0.1", {"start": v(20.08, 19.09) * mm, "end": v(21.62, 13.34) * mm});
            skLineSegment(sketch, "E39.0.3", {"start": v(21.62, 13.34) * mm, "end": v(20.08, 19.09) * mm});
            skArc(sketch, "E40", {"start": v(20.08, 19.09) * mm, "mid": v(25, 15.31) * mm, "end": v(29.92, 19.09) * mm});
            skPoint(sketch, "E38.0.0.end.orphan", {"position": v(32.28, 27.9) * mm});
            skPoint(sketch, "E41.orphan", {"position": v(31.38, 24.52) * mm});
            skPoint(sketch, "E39.0.0.end.orphan", {"position": v(17.72, 27.9) * mm});
            skPoint(sketch, "E39.0.0.start.orphan", {"position": v(18.62, 24.52) * mm});
            skSolve(sketch);
        }
        {
            var Q0;
            Q0 = qSketchRegion(id + "F25", true);
            extrude(context, id + "F26", {"entities" : qUnion([Q0]), "operationType" : NewBodyOperationType.ADD, "endBound" : BoundingType.SYMMETRIC, "depth" : 1 * mm});
        }
    });
